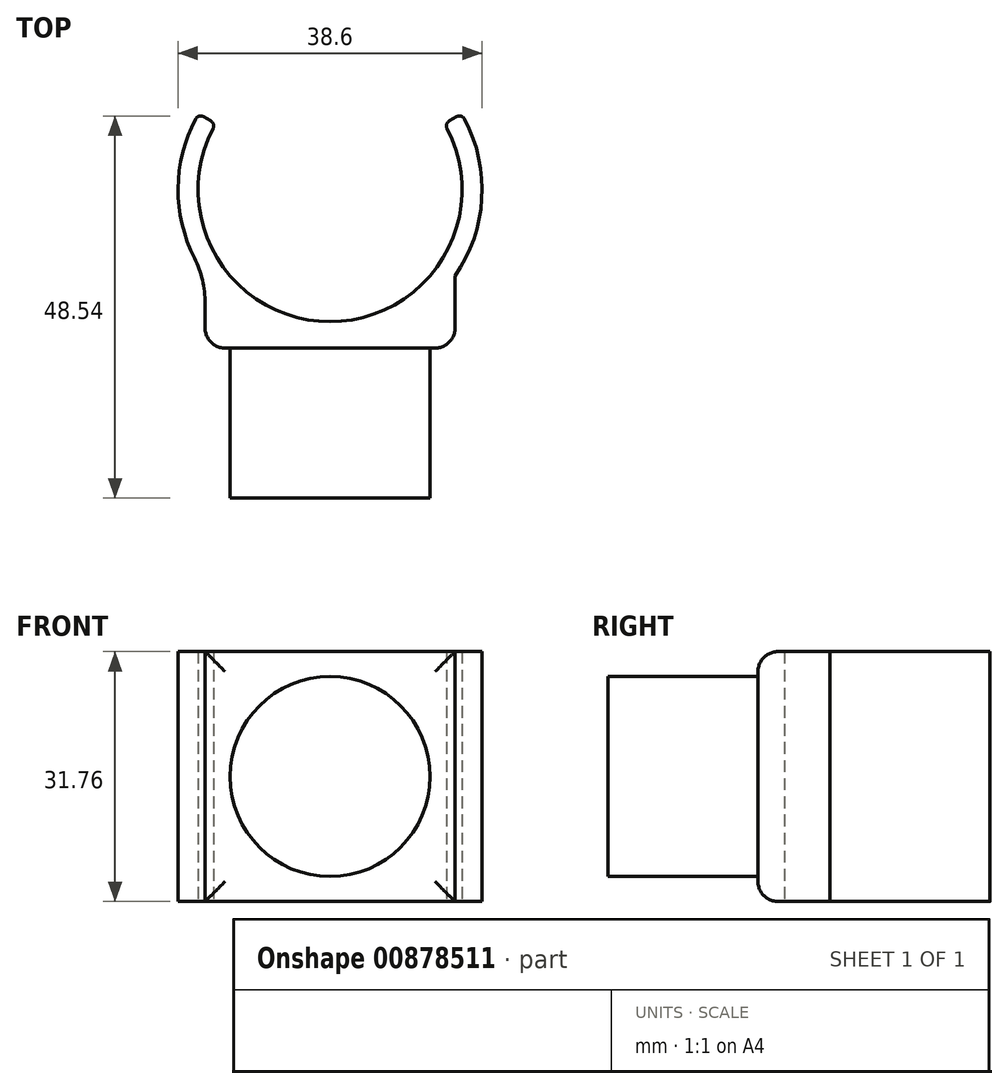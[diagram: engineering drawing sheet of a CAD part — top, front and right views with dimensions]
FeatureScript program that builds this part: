
annotation { "Feature Type Name" : "Feature", "Feature Type Description" : "" }
export const myFeature = defineFeature(function(context is Context, id is Id, definition is map)
    precondition{}
    {
        {
            var Q0;
            Q0=qCreatedBy(makeId("Top.planeOp"),FACE);
            var sketch = newSketch(context, id + "F0", { "sketchPlane" : qUnion([Q0])});
            skCircle(sketch, "E0", {"center": v(0, 0) * mm, "radius": 19.3 * mm});
            skCircle(sketch, "E1", {"center": v(0, 0) * mm, "radius": 16.76 * mm});
            skLineSegment(sketch, "E2", {"start": v(-53.94, 0) * mm, "end": v(51.47, 0) * mm, "construction": true});
            skLineSegment(sketch, "E3", {"start": v(0, 37.95) * mm, "end": v(0, -48.77) * mm, "construction": true});
            skLineSegment(sketch, "E4", {"start": v(0, 0) * mm, "end": v(-16.72, 9.65) * mm});
            skLineSegment(sketch, "E5.MirrorCS", {"start": v(0, 0) * mm, "end": v(16.72, 9.65) * mm});
            skLineSegment(sketch, "E6.top", {"start": v(-15.88, -20.12) * mm, "end": v(15.88, -20.12) * mm});
            skLineSegment(sketch, "E6.left", {"start": v(-15.87, -10.98) * mm, "end": v(-15.87, -20.12) * mm});
            skLineSegment(sketch, "E6.right", {"start": v(15.88, -10.98) * mm, "end": v(15.88, -20.12) * mm});
            skPoint(sketch, "E6.middle", {"position": v(0, -15.55) * mm});
            skSolve(sketch);
        }
        {
            var Q0;
            {var subQ0=sQuery(id+"F0.wireOp",EDGE,"E4");var subQ5=sQuery(id+"F0.wireOp",EDGE,"E0");var subQ9=makeQuery(id+"F0.imprint","INTERSECT",VERTEX,{"derivedFrom":[subQ5,subQ0]});Q0=makeQuery(id+"F0.imprint","IMPRINT",FACE,{"disambiguationData":[TD([[makeQuery(id+"F0.imprint","IMPRINT",EDGE,{"disambiguationData":[TD([[subQ9,-1.0]])],"derivedFrom":subQ5}),1.0]])]});}
            extrude(context, id + "F1", {"entities" : qUnion([Q0]), "endBound" : BoundingType.SYMMETRIC, "depth" : 31.75 * mm, "offsetDistance" : 25.4 * mm});
        }
        {
            var Q0;
            Q0=makeQuery(id+"F0.imprint","IMPRINT",FACE,{"disambiguationData":[TD([[makeQuery(id+"F0.imprint","IMPRINT",EDGE,{"derivedFrom":sQuery(id+"F0.wireOp",EDGE,"E6.top")}),1.0]])]});
            extrude(context, id + "F2", {"entities" : qUnion([Q0]), "operationType" : NewBodyOperationType.ADD, "endBound" : BoundingType.SYMMETRIC, "depth" : 31.75 * mm, "offsetDistance" : 25.4 * mm});
        }
        {
            var Q0;
            Q0=makeQuery(id+"F2.opExtrude","SWEPT_FACE",FACE,{"disambiguationData":[OSD([sQuery(id+"F0.wireOp",EDGE,"E6.top")])]});
            var sketch = newSketch(context, id + "F3", { "sketchPlane" : qUnion([Q0])});
            skCircle(sketch, "E7", {"center": v(0, 0) * mm, "radius": 12.7 * mm});
            skSolve(sketch);
        }
        {
            var Q0;
            Q0 = qSketchRegion(id + "F3", true);
            extrude(context, id + "F4", {"entities" : qUnion([Q0]), "operationType" : NewBodyOperationType.ADD, "depth" : 19.05 * mm, "offsetDistance" : 25.4 * mm});
        }
        {
            var Q0;
            Q0=makeQuery(id+"F2.opExtrude","SWEPT_EDGE",EDGE,{"disambiguationData":[OSD([sQuery(id+"F0.wireOp",EDGE,"E6.top"),sQuery(id+"F0.wireOp",EDGE,"E6.left")])]});
            var Q1;
            Q1=makeQuery(id+"F2.opExtrude","SWEPT_EDGE",EDGE,{"disambiguationData":[OSD([sQuery(id+"F0.wireOp",EDGE,"E6.top"),sQuery(id+"F0.wireOp",EDGE,"E6.right")])]});
            var Q2;
            Q2=makeQuery(id+"F2.opExtrude","CAP_EDGE",EDGE,{"disambiguationData":[OSD([sQuery(id+"F0.wireOp",EDGE,"E6.top")])],"isStart":false});
            var Q3;
            Q3=makeQuery(id+"F2.opExtrude","CAP_EDGE",EDGE,{"disambiguationData":[OSD([sQuery(id+"F0.wireOp",EDGE,"E6.top")])],"isStart":true});
            fillet(context, id + "F5", {"entities" : qUnion([Q0, Q1, Q2, Q3]), "radius" : 2.54 * mm, "tangentPropagation" : true, "allowEdgeOverflow" : false});
        }
        {
            var Q0;
            Q0=makeQuery(id+"F2.opExtrude","SWEPT_EDGE",EDGE,{"disambiguationData":[OSD([sQuery(id+"F0.wireOp",EDGE,"E0"),sQuery(id+"F0.wireOp",EDGE,"E6.left")])]});
            var Q1;
            Q1=makeQuery(id+"F2.opExtrude","SWEPT_EDGE",EDGE,{"disambiguationData":[OSD([sQuery(id+"F0.wireOp",EDGE,"E0"),sQuery(id+"F0.wireOp",EDGE,"E6.right")])]});
            fillet(context, id + "F6", {"entities" : qUnion([Q0, Q1]), "radius" : 12.7 * mm, "tangentPropagation" : true, "allowEdgeOverflow" : false});
        }
        {
            var Q0;
            Q0=makeQuery(id+"F1.opExtrude","SWEPT_EDGE",EDGE,{"disambiguationData":[OSD([sQuery(id+"F0.wireOp",EDGE,"E0"),sQuery(id+"F0.wireOp",EDGE,"E4")])]});
            var Q1;
            Q1=makeQuery(id+"F1.opExtrude","SWEPT_EDGE",EDGE,{"disambiguationData":[OSD([sQuery(id+"F0.wireOp",EDGE,"E1"),sQuery(id+"F0.wireOp",EDGE,"E4")])]});
            var Q2;
            Q2=makeQuery(id+"F1.opExtrude","SWEPT_EDGE",EDGE,{"disambiguationData":[OSD([sQuery(id+"F0.wireOp",EDGE,"E0"),sQuery(id+"F0.wireOp",EDGE,"E5.MirrorCS")])]});
            var Q3;
            Q3=makeQuery(id+"F1.opExtrude","SWEPT_EDGE",EDGE,{"disambiguationData":[OSD([sQuery(id+"F0.wireOp",EDGE,"E1"),sQuery(id+"F0.wireOp",EDGE,"E5.MirrorCS")])]});
            fillet(context, id + "F7", {"entities" : qUnion([Q0, Q1, Q2, Q3]), "radius" : 0.76 * mm, "tangentPropagation" : true, "allowEdgeOverflow" : false});
        }
    });
